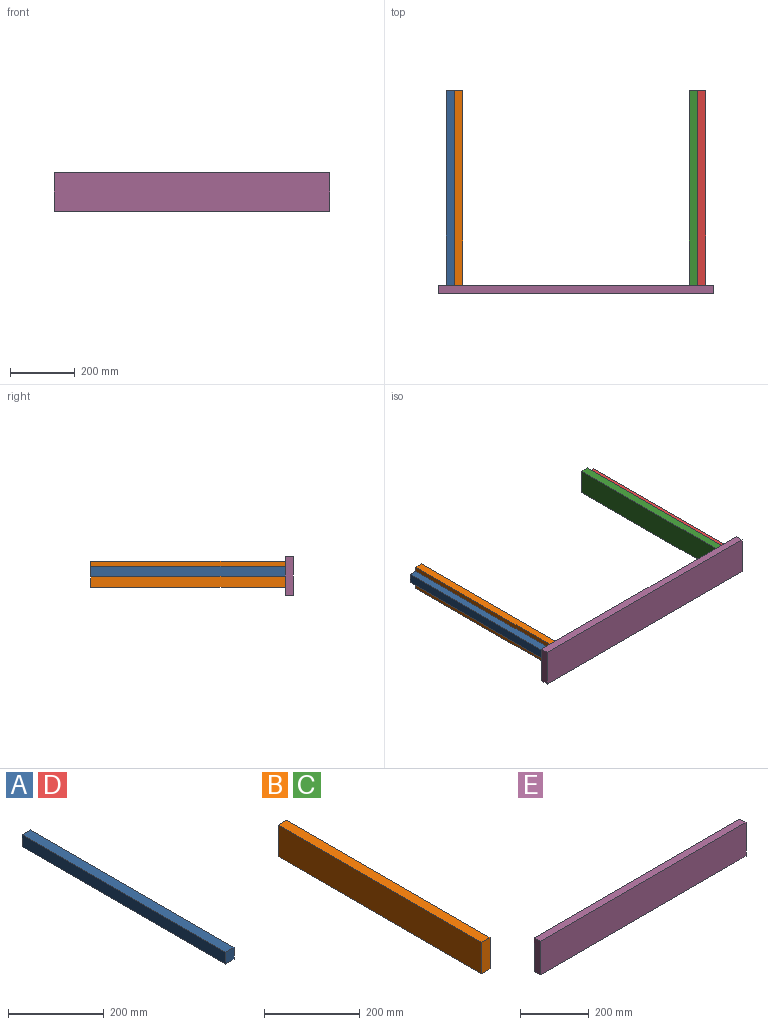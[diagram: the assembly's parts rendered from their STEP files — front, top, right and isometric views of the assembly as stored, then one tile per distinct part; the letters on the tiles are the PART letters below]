
ASSEMBLY  parts=5 mates=4
PART A: 6 faces, bbox 25x600x30 mm
  f0: plane 600x30mm, normal (-1,0,0), area 18000mm2, adj f1,f3,f4,f5
  f1: plane 600x25mm, normal (0,0,-1), area 15000mm2, adj f0,f2,f4,f5
  f2: plane 600x30mm, normal (1,0,0), area 18000mm2, adj f1,f3,f4,f5
  f3: plane 600x25mm, normal (0,0,1), area 15000mm2, adj f0,f2,f4,f5
  f4: plane 30x25mm, normal (0,-1,0), area 750mm2, adj f0,f1,f2,f3
  f5: plane 30x25mm, normal (0,1,0), area 750mm2, adj f0,f1,f2,f3
PART B: 6 faces, bbox 25x600x80 mm
  f0: plane 600x80mm, normal (-1,0,0), area 48000mm2, adj f1,f3,f4,f5
  f1: plane 600x25mm, normal (0,0,-1), area 15000mm2, adj f0,f2,f4,f5
  f2: plane 600x80mm, normal (1,0,0), area 48000mm2, adj f1,f3,f4,f5
  f3: plane 600x25mm, normal (0,0,1), area 15000mm2, adj f0,f2,f4,f5
  f4: plane 80x25mm, normal (0,-1,0), area 2000mm2, adj f0,f1,f2,f3
  f5: plane 80x25mm, normal (0,1,0), area 2000mm2, adj f0,f1,f2,f3
PART C: same geometry as B
PART D: same geometry as A
PART E: 6 faces, bbox 850x25x120 mm
  f0: plane 120x25mm, normal (1,0,0), area 3000mm2, adj f1,f3,f4,f5
  f1: plane 850x25mm, normal (0,0,1), area 21250mm2, adj f0,f2,f4,f5
  f2: plane 120x25mm, normal (-1,0,0), area 3000mm2, adj f1,f3,f4,f5
  f3: plane 850x25mm, normal (0,0,-1), area 21250mm2, adj f0,f2,f4,f5
  f4: plane 850x120mm, normal (0,-1,0), area 102000mm2, adj f0,f1,f2,f3
  f5: plane 850x120mm, normal (0,1,0), area 102000mm2, adj f0,f1,f2,f3
PLACE A t=(-154.68,535.69,235.87)mm
PLACE B t=(-879.68,535.69,230.87)mm
PLACE C t=(-154.68,535.69,230.87)mm
PLACE D t=(620.32,535.69,235.87)mm
PLACE E t=(-154.68,-64.31,18.74)mm
MATE fastened C.f4 <-> E.f5  axis (0,-1,0) through (220.32,-64.31,23.74)mm
MATE fastened B.f4 <-> E.f5  axis (0,-1,0) through (-529.68,-64.31,23.74)mm
MATE fastened D.f5 <-> C.f5  axis (0,1,0) through (220.32,535.69,33.74)mm
MATE fastened A.f5 <-> B.f5  axis (0,1,0) through (-529.68,535.69,33.74)mm
